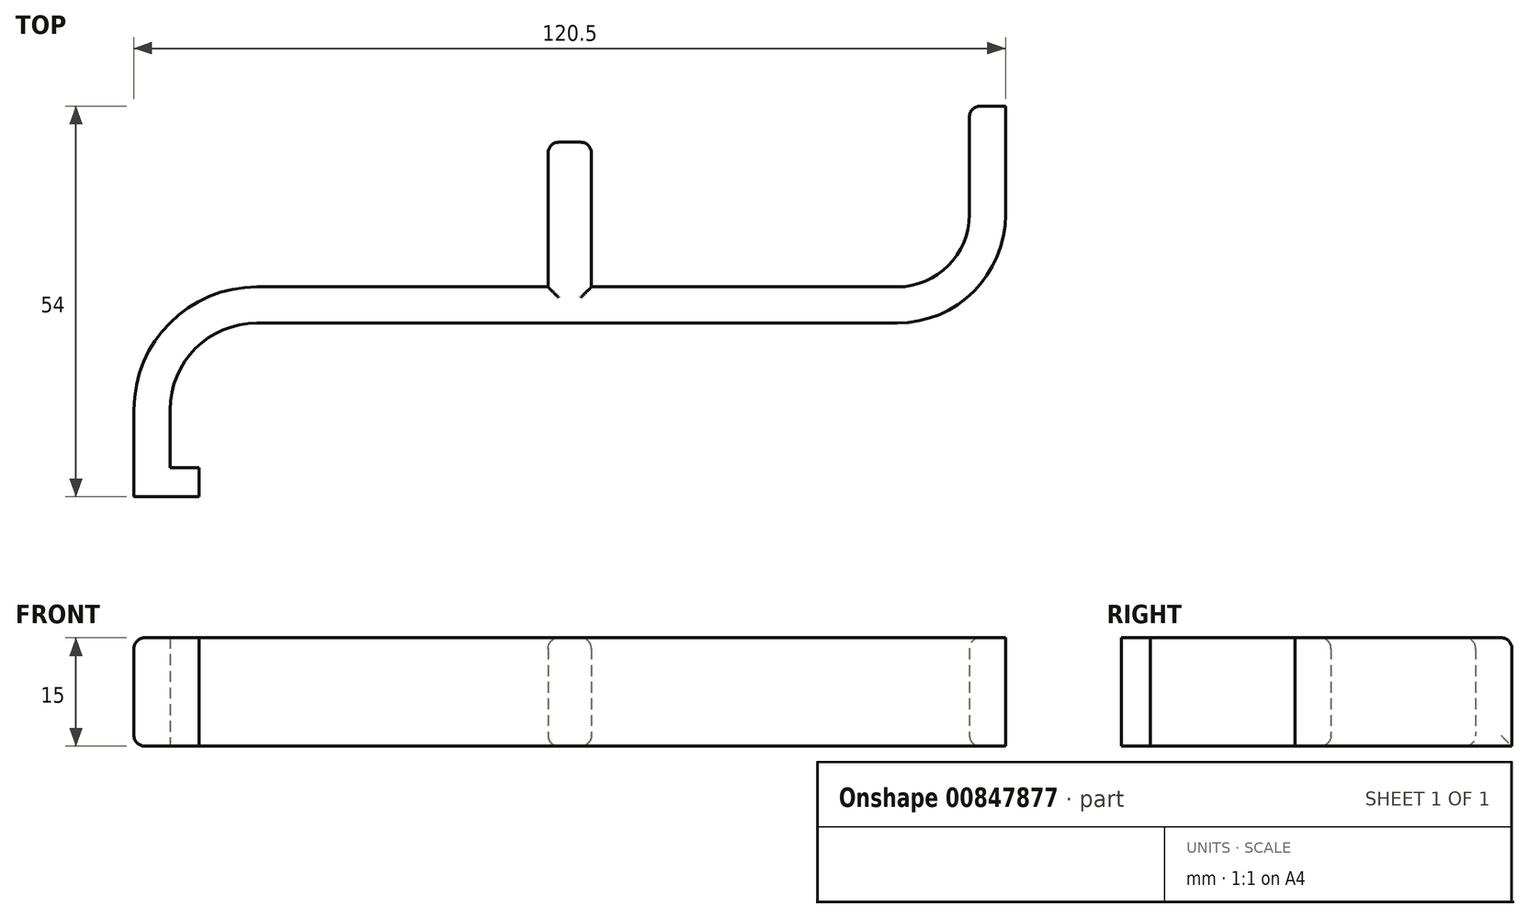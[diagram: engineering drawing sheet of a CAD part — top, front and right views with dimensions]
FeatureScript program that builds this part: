
annotation { "Feature Type Name" : "Feature", "Feature Type Description" : "" }
export const myFeature = defineFeature(function(context is Context, id is Id, definition is map)
    precondition{}
    {
        {
            var Q0;
            Q0=qCreatedBy(makeId("Top.planeOp"),FACE);
            var sketch = newSketch(context, id + "F0", { "sketchPlane" : qUnion([Q0])});
            skLineSegment(sketch, "E0", {"start": v(-90.02, 29) * mm, "end": v(-49.77, 29) * mm});
            skLineSegment(sketch, "E1", {"start": v(8.48, 39) * mm, "end": v(8.48, 54) * mm});
            skLineSegment(sketch, "E2", {"start": v(8.48, 54) * mm, "end": v(13.48, 54) * mm});
            skLineSegment(sketch, "E3", {"start": v(13.48, 54) * mm, "end": v(13.48, 39) * mm});
            skLineSegment(sketch, "E4", {"start": v(-1.52, 24) * mm, "end": v(-90.02, 24) * mm});
            skLineSegment(sketch, "E5", {"start": v(-102.02, 12) * mm, "end": v(-102.02, 4) * mm});
            skLineSegment(sketch, "E6", {"start": v(-102.02, 0) * mm, "end": v(-107.02, 0) * mm});
            skLineSegment(sketch, "E7", {"start": v(-107.02, 0) * mm, "end": v(-107.02, 12) * mm});
            skLineSegment(sketch, "E8", {"start": v(-49.77, 29) * mm, "end": v(-49.77, 49) * mm});
            skLineSegment(sketch, "E9", {"start": v(-49.77, 49) * mm, "end": v(-43.77, 49) * mm});
            skLineSegment(sketch, "E10", {"start": v(-43.77, 49) * mm, "end": v(-43.77, 29) * mm});
            skLineSegment(sketch, "E11.trimOffspring", {"start": v(-43.77, 29) * mm, "end": v(-1.52, 29) * mm});
            skLineSegment(sketch, "E12", {"start": v(-102.02, -6.99) * mm, "end": v(8.48, -6.99) * mm, "construction": true});
            skPoint(sketch, "E13", {"position": v(-46.77, -6.99) * mm});
            skPoint(sketch, "E14", {"position": v(-46.77, 49) * mm});
            skPoint(sketch, "E15.visualSharp", {"position": v(-102.02, 24) * mm});
            skArc(sketch, "E15.filletArc", {"start": v(-90.02, 24) * mm, "mid": v(-98.5, 20.49) * mm, "end": v(-102.02, 12) * mm});
            skPoint(sketch, "E16.visualSharp", {"position": v(8.48, 29) * mm});
            skArc(sketch, "E16.filletArc", {"start": v(-1.52, 29) * mm, "mid": v(5.55, 31.93) * mm, "end": v(8.48, 39) * mm});
            skArc(sketch, "E17", {"start": v(-90.02, 29) * mm, "mid": v(-102.04, 24.02) * mm, "end": v(-107.02, 12) * mm});
            skArc(sketch, "E18", {"start": v(-1.52, 24) * mm, "mid": v(9.09, 28.4) * mm, "end": v(13.48, 39) * mm});
            skLineSegment(sketch, "E19.bottom", {"start": v(-102.02, 0) * mm, "end": v(-98.02, 0) * mm});
            skLineSegment(sketch, "E19.top", {"start": v(-102.02, 4) * mm, "end": v(-98.02, 4) * mm});
            skLineSegment(sketch, "E19.right", {"start": v(-98.02, 0) * mm, "end": v(-98.02, 4) * mm});
            skSolve(sketch);
        }
        {
            var Q0;
            Q0 = qSketchRegion(id + "F0", true);
            extrude(context, id + "F1", {"entities" : qUnion([Q0]), "depth" : 15 * mm, "offsetDistance" : 25 * mm});
        }
        {
            var Q0;
            Q0=makeQuery(id+"F1.opExtrude","CAP_EDGE",EDGE,{"disambiguationData":[OSD([sQuery(id+"F0.wireOp",EDGE,"E16.filletArc")])],"isStart":true});
            var Q1;
            Q1=makeQuery(id+"F1.opExtrude","CAP_EDGE",EDGE,{"disambiguationData":[OSD([sQuery(id+"F0.wireOp",EDGE,"E10")])],"isStart":true});
            var Q2;
            Q2=makeQuery(id+"F1.opExtrude","CAP_EDGE",EDGE,{"disambiguationData":[OSD([sQuery(id+"F0.wireOp",EDGE,"E8")])],"isStart":true});
            var Q3;
            Q3=makeQuery(id+"F1.opExtrude","CAP_EDGE",EDGE,{"disambiguationData":[OSD([sQuery(id+"F0.wireOp",EDGE,"E0")])],"isStart":true});
            var Q4;
            Q4=makeQuery(id+"F1.opExtrude","CAP_EDGE",EDGE,{"disambiguationData":[OSD([sQuery(id+"F0.wireOp",EDGE,"E9")])],"isStart":true});
            var Q5;
            Q5=makeQuery(id+"F1.opExtrude","CAP_EDGE",EDGE,{"disambiguationData":[OSD([sQuery(id+"F0.wireOp",EDGE,"E17")])],"isStart":false});
            var Q6;
            Q6=makeQuery(id+"F1.opExtrude","CAP_EDGE",EDGE,{"disambiguationData":[OSD([sQuery(id+"F0.wireOp",EDGE,"E7")])],"isStart":false});
            var Q7;
            Q7=makeQuery(id+"F1.opExtrude","CAP_EDGE",EDGE,{"disambiguationData":[OSD([sQuery(id+"F0.wireOp",EDGE,"E8")])],"isStart":false});
            var Q8;
            Q8=makeQuery(id+"F1.opExtrude","CAP_EDGE",EDGE,{"disambiguationData":[OSD([sQuery(id+"F0.wireOp",EDGE,"E9")])],"isStart":false});
            var Q9;
            Q9=makeQuery(id+"F1.opExtrude","CAP_EDGE",EDGE,{"disambiguationData":[OSD([sQuery(id+"F0.wireOp",EDGE,"E10")])],"isStart":false});
            var Q10;
            Q10=makeQuery(id+"F1.opExtrude","CAP_EDGE",EDGE,{"disambiguationData":[OSD([sQuery(id+"F0.wireOp",EDGE,"E11.trimOffspring")])],"isStart":false});
            var Q11;
            Q11=makeQuery(id+"F1.opExtrude","CAP_EDGE",EDGE,{"disambiguationData":[OSD([sQuery(id+"F0.wireOp",EDGE,"E2")])],"isStart":false});
            var Q12;
            Q12=makeQuery(id+"F1.opExtrude","SWEPT_EDGE",EDGE,{"disambiguationData":[OSD([sQuery(id+"F0.wireOp",EDGE,"E8"),sQuery(id+"F0.wireOp",EDGE,"E9")])]});
            var Q13;
            Q13=makeQuery(id+"F1.opExtrude","SWEPT_EDGE",EDGE,{"disambiguationData":[OSD([sQuery(id+"F0.wireOp",EDGE,"E9"),sQuery(id+"F0.wireOp",EDGE,"E10")])]});
            var Q14;
            Q14=makeQuery(id+"F1.opExtrude","SWEPT_EDGE",EDGE,{"disambiguationData":[OSD([sQuery(id+"F0.wireOp",EDGE,"E1"),sQuery(id+"F0.wireOp",EDGE,"E2")])]});
            fillet(context, id + "F2", {"entities" : qUnion([Q0, Q1, Q2, Q3, Q4, Q5, Q6, Q7, Q8, Q9, Q10, Q11, Q12, Q13, Q14]), "radius" : 1.5 * mm, "tangentPropagation" : true, "allowEdgeOverflow" : false});
        }
    });
